# Revit family: Drain_Channel_Nero_TileInsert_89mmOutlet
name_source: partatom
category: Plumbing Fixtures
units: mm (PartAtom-declared; Revit-internal decimal feet)

## family parameters
Always vertical = Yes
Cut with Voids When Loaded = Yes
Maintain Annotation Orientation = No
OmniClass Number = 23.31.11.00
OmniClass Title = Faucets
Part Type = Normal
Room Calculation Point = No
Round Connector Dimension = Use Diameter
Shared = No
Work Plane-Based = No

## types (10) — shared parameters
Assembly Code = D2010
CW Connection = Yes
HW Connection = Yes
IfcExportAs = IfcFurnitureType
IfcExportType = USERDEFINED
Manufacturer = Nero
ManufacturerOverallDepth = 106 mm  [stored 0.347769 ft]
ManufacturerOverallHeight = 76 mm
ManufacturerURLProductSpecific = https://nerotapware.com.au
ModifiedIssue = 20251105 $
URL = https://nerotapware.com.au
Uniclass2015Code = Pr_65_52_24_24
Uniclass2015Title = Drainage channels with gratings
Uniclass2015Version = Products v1.35
Vent Connection = No
Waste Connection = No
zero-valued in all types: CWFU, Default Elevation, HWFU, WFU

## per-type parameters (varying)
| type | Description | ManufacturerOverallWidth | ManufacturerSpecCode | Material | Model | Type Comments |
| Brushed Gold (NRFG005HSBG) | Tile Insert V Channel 1200mm Floor Grate 89mm Outlet With Hole Saw Brushed Gold | 1200 mm | NRFG005HSBG | Metal_Gold_Nero_Brushed | NRFG005HSBG | Drain - Channel - 89mm Outlet - Brushed Gold |
| Matte Black (NRFG005HSMB) | Tile Insert V Channel 1200mm Floor Grate 89mm Outlet With Hole Saw Matte Black | 1200 mm | NRFG005HSMB | Metal_MatteBlack_Nero | NRFG005HSMB | Drain - Channel - 89mm Outlet - Matte Black |
| Brushed Nickel (NRFG005HSBN) | Tile Insert V Channel 1200mm Floor Grate 89mm Outlet With Hole Saw Brushed Nickel | 1200 mm | NRFG005HSBN | Metal_Nickel_Nero_Brushed | NRFG005HSBN | Drain - Channel - 89mm Outlet - Brushed Nickel |
| Brushed Bronze (NRFG005HSBZ) | Tile Insert V Channel 1200mm Floor Grate 89mm Outlet With Hole Saw Brushed Bronze | 1200 mm | NRFG005HSBZ | Metal_Bronze_Nero_Brushed | NRFG005HSBZ | Drain - Channel - 89mm Outlet - Brushed Bronze |
| Gunmetal (NRFG005HSGM) | Tile Insert V Channel 1200mm Floor Grate 89mm Outlet With Hole Saw Gun Metal | 1200 mm | NRFG005HSGM | Metal_GunMetal_Nero | NRFG005HSGM | Drain - Channel - 89mm Outlet - Gunmetal |
| Brushed Nickel (NRFG004HSBN) | Tile Insert V Channel 600mm Floor Grate 89mm Outlet With Hole Saw Brushed Nickel | 600 mm | NRFG004HSBN | Metal_Nickel_Nero_Brushed | NRFG004HSBN | Drain - Channel - 89mm Outlet - Brushed Nickel |
| Brushed Bronze (NRFG004HSBZ) | Tile Insert V Channel 600mm Floor Grate 89mm Outlet With Hole Saw Brushed Bronze | 600 mm | NRFG004HSBZ | Metal_Bronze_Nero_Brushed | NRFG004HSBZ | Drain - Channel - 89mm Outlet - Brushed Bronze |
| Brushed Gold (NRFG004HSBG) | Tile Insert V Channel 600mm Floor Grate 89mm Outlet With Hole Saw Brushed Gold | 600 mm | NRFG004HSBG | Metal_Gold_Nero_Brushed | NRFG004HSBG | Drain - Channel - 89mm Outlet - Brushed Gold |
| Matte Black (NRFG004HSMB) | Tile Insert V Channel 600mm Floor Grate 89mm Outlet With Hole Saw Matte Black | 600 mm | NRFG004HSMB | Metal_MatteBlack_Nero | NRFG004HSMB | Drain - Channel - 89mm Outlet - Matte Black |
| Gunmetal (NRFG004HSGM) | Tile Insert V Channel 600mm Floor Grate 89mm Outlet With Hole Saw Gun Metal | 600 mm | NRFG004HSGM | Metal_GunMetal_Nero | NRFG004HSGM | Drain - Channel - 89mm Outlet - Gunmetal |

note: [stored X ft] marks values corroborated as IEEE doubles in the binary element streams (Revit-internal decimal feet)

## geometry (parser evidence)
native form markers: Sweep x2
no freeform markers — native parametric forms only
